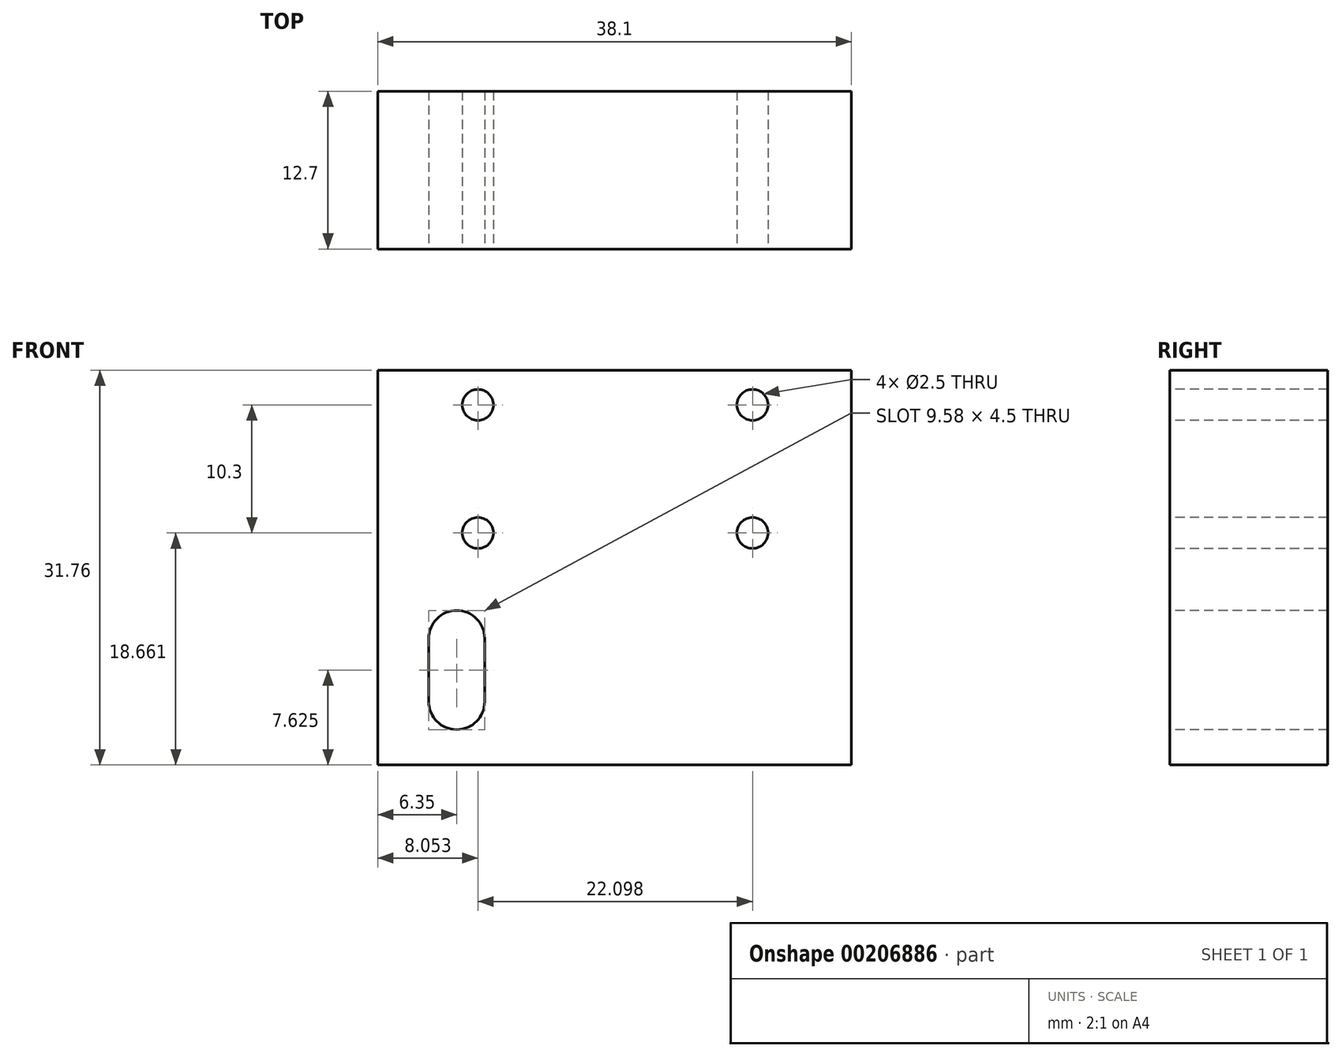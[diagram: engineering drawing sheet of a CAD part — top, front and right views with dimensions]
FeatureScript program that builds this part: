
annotation { "Feature Type Name" : "Feature", "Feature Type Description" : "" }
export const myFeature = defineFeature(function(context is Context, id is Id, definition is map)
    precondition{}
    {
        {
            var Q0;
            Q0=qCreatedBy(makeId("Front.planeOp"),FACE);
            var sketch = newSketch(context, id + "F0", { "sketchPlane" : qUnion([Q0])});
            skLineSegment(sketch, "E0.bottom", {"start": v(19.05, -15.88) * mm, "end": v(-19.05, -15.88) * mm});
            skLineSegment(sketch, "E0.top", {"start": v(19.05, 15.88) * mm, "end": v(-19.05, 15.87) * mm});
            skLineSegment(sketch, "E0.left", {"start": v(19.05, -15.88) * mm, "end": v(19.05, 15.88) * mm});
            skLineSegment(sketch, "E0.right", {"start": v(-19.05, -15.88) * mm, "end": v(-19.05, 15.87) * mm});
            skPoint(sketch, "E0.middle", {"position": v(0, 0) * mm});
            skSolve(sketch);
        }
        {
            var Q0;
            Q0=qSketchRegion(id+"F0",true);
            extrude(context, id + "F1", {"entities" : qUnion([Q0]), "endBound" : BoundingType.SYMMETRIC, "depth" : 12.7 * mm});
        }
        {
            var Q0;
            Q0=makeQuery(id+"F1.opExtrude","CAP_FACE",FACE,{"disambiguationData":[OSD([sQuery(id+"F0.wireOp",EDGE,"E0.bottom"),sQuery(id+"F0.wireOp",EDGE,"E0.top"),sQuery(id+"F0.wireOp",EDGE,"E0.left"),sQuery(id+"F0.wireOp",EDGE,"E0.right")])],"isStart":false});
            var sketch = newSketch(context, id + "F2", { "sketchPlane" : qUnion([Q0])});
            skPoint(sketch, "E1", {"position": v(11.1, 13.08) * mm});
            skPoint(sketch, "E2", {"position": v(-11, 2.78) * mm});
            skPoint(sketch, "E3", {"position": v(-11, 13.08) * mm});
            skPoint(sketch, "E4", {"position": v(11.1, 2.78) * mm});
            skSolve(sketch);
        }
        {
            var Q0;
            Q0=sQuery(id+"F2.wireOp",VERTEX,"E2");
            var Q1;
            Q1=sQuery(id+"F2.wireOp",VERTEX,"E1");
            var Q2;
            Q2=sQuery(id+"F2.wireOp",VERTEX,"E3");
            var Q3;
            Q3=sQuery(id+"F2.wireOp",VERTEX,"E4");
            var Q4;
            Q4=makeQuery(id+"F1.opExtrude","SWEPT_BODY",BODY,{"disambiguationData":[OSD([sQuery(id+"F0.wireOp",EDGE,"E0.bottom"),sQuery(id+"F0.wireOp",EDGE,"E0.top"),sQuery(id+"F0.wireOp",EDGE,"E0.left"),sQuery(id+"F0.wireOp",EDGE,"E0.right")])]});
            hole(context, id + "F3", {"style" : HoleStyle.SIMPLE, "endStyle" : HoleEndStyle.THROUGH, "standardTappedOrClearance" : lookupTablePath({ "standard" : "ISO", "engagement" : "75%", "pitch" : "0.5 mm", "size" : "M3", "type" : "Tapped" }), "standardBlindInLast" : lookupTablePath({ "standard" : "ISO", "engagement" : "75%", "pitch" : "0.5 mm", "size" : "M3", "type" : "Tapped" }), "holeDiameter" : 2.5 * mm, "locations" : qUnion([Q0, Q1, Q2, Q3]), "scope" : qUnion([Q4]), "isTappedThrough" : true, "majorDiameter" : 3 * mm, "showTappedDepth" : true});
        }
        {
            var Q0;
            Q0=makeQuery(id+"F1.opExtrude","CAP_FACE",FACE,{"disambiguationData":[OSD([sQuery(id+"F0.wireOp",EDGE,"E0.bottom"),sQuery(id+"F0.wireOp",EDGE,"E0.top"),sQuery(id+"F0.wireOp",EDGE,"E0.left"),sQuery(id+"F0.wireOp",EDGE,"E0.right")])],"isStart":false});
            var sketch = newSketch(context, id + "F4", { "sketchPlane" : qUnion([Q0])});
            skLineSegment(sketch, "E5", {"start": v(-12.7, -5.72) * mm, "end": v(-12.7, -10.8) * mm});
            skArc(sketch, "E6.0.startCap", {"start": v(-14.95, -5.72) * mm, "mid": v(-12.7, -3.47) * mm, "end": v(-10.45, -5.72) * mm});
            skArc(sketch, "E6.0.endCap", {"start": v(-10.45, -10.8) * mm, "mid": v(-12.7, -13.05) * mm, "end": v(-14.95, -10.8) * mm});
            skLineSegment(sketch, "E6.0.left", {"start": v(-10.45, -5.72) * mm, "end": v(-10.45, -10.8) * mm});
            skLineSegment(sketch, "E6.0.right", {"start": v(-14.95, -5.72) * mm, "end": v(-14.95, -10.8) * mm});
            skSolve(sketch);
        }
        {
            var Q0;
            Q0=qSketchRegion(id+"F4",true);
            extrude(context, id + "F5", {"entities" : qUnion([Q0]), "operationType" : NewBodyOperationType.REMOVE, "endBound" : BoundingType.UP_TO_NEXT, "oppositeDirection" : true, "depth" : 25.4 * mm});
        }
    });
